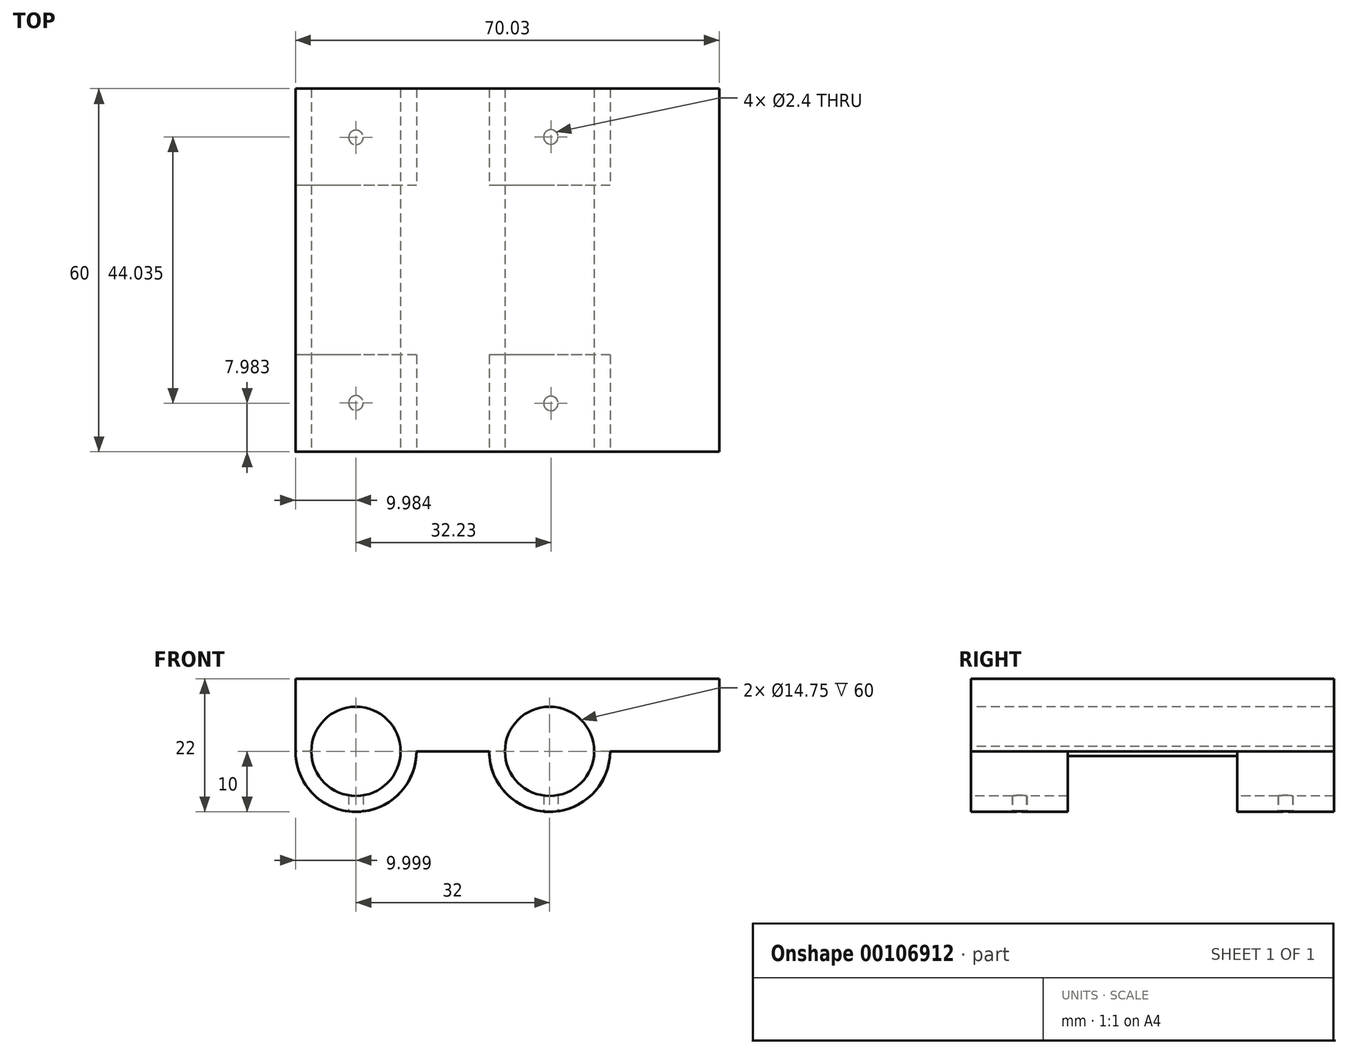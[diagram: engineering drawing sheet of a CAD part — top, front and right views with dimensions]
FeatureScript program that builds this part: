
annotation { "Feature Type Name" : "Feature", "Feature Type Description" : "" }
export const myFeature = defineFeature(function(context is Context, id is Id, definition is map)
    precondition{}
    {
        {
            var Q0;
            Q0=qCreatedBy(makeId("Top.planeOp"),FACE);
            var sketch = newSketch(context, id + "F0", { "sketchPlane" : qUnion([Q0])});
            skLineSegment(sketch, "E0.bottom", {"start": v(35, -30) * mm, "end": v(-35, -30) * mm});
            skLineSegment(sketch, "E0.top", {"start": v(35, 30) * mm, "end": v(-35, 30) * mm});
            skLineSegment(sketch, "E0.left", {"start": v(35, -30) * mm, "end": v(35, 30) * mm});
            skLineSegment(sketch, "E0.right", {"start": v(-35, -30) * mm, "end": v(-35, 30) * mm});
            skPoint(sketch, "E0.middle", {"position": v(0, 0) * mm});
            skSolve(sketch);
        }
        {
            var Q0;
            Q0 = qSketchRegion(id + "F0", true);
            extrude(context, id + "F1", {"entities" : qUnion([Q0]), "depth" : 12 * mm});
        }
        {
            var Q0;
            Q0=makeQuery(id+"F1.opExtrude","SWEPT_FACE",FACE,{"disambiguationData":[OSD([sQuery(id+"F0.wireOp",EDGE,"E0.bottom")])]});
            var sketch = newSketch(context, id + "F2", { "sketchPlane" : qUnion([Q0])});
            skCircle(sketch, "E1", {"center": v(-25.03, 0) * mm, "radius": 10 * mm});
            skCircle(sketch, "E2", {"center": v(6.97, 0) * mm, "radius": 10 * mm});
            skLineSegment(sketch, "E3", {"start": v(-35, 0) * mm, "end": v(-15.03, 0) * mm, "construction": true});
            skLineSegment(sketch, "E4", {"start": v(-3.03, 0) * mm, "end": v(16.97, 0) * mm, "construction": true});
            skCircle(sketch, "E5", {"center": v(-25.03, 0) * mm, "radius": 7.38 * mm});
            skCircle(sketch, "E6", {"center": v(6.97, 0) * mm, "radius": 7.38 * mm});
            skSolve(sketch);
        }
        {
            var Q0;
            {var subQ0=sQuery(id+"F2.wireOp",EDGE,"E5");var subQ1=makeQuery(id+"F1.opExtrude","CAP_EDGE",EDGE,{"disambiguationData":[OSD([sQuery(id+"F0.wireOp",EDGE,"E0.bottom")])],"isStart":true});var subQ2=makeQuery(id+"F2.imprint","INTERSECT",VERTEX,{"disambiguationData":[OD(0.0)],"derivedFrom":[subQ1,subQ0]});Q0=makeQuery(id+"F2.imprint","IMPRINT",FACE,{"disambiguationData":[TD([[makeQuery(id+"F2.imprint","IMPRINT",EDGE,{"disambiguationData":[TD([[subQ2,1.0]])],"derivedFrom":subQ0}),1.0]])]});}
            var Q1;
            {var subQ0=sQuery(id+"F2.wireOp",EDGE,"E6");var subQ1=makeQuery(id+"F1.opExtrude","CAP_EDGE",EDGE,{"disambiguationData":[OSD([sQuery(id+"F0.wireOp",EDGE,"E0.bottom")])],"isStart":true});var subQ2=makeQuery(id+"F2.imprint","INTERSECT",VERTEX,{"disambiguationData":[OD(0.0)],"derivedFrom":[subQ1,subQ0]});Q1=makeQuery(id+"F2.imprint","IMPRINT",FACE,{"disambiguationData":[TD([[makeQuery(id+"F2.imprint","IMPRINT",EDGE,{"disambiguationData":[TD([[subQ2,-1.0]])],"derivedFrom":subQ0}),1.0]])]});}
            extrude(context, id + "F3", {"entities" : qUnion([Q0, Q1]), "operationType" : NewBodyOperationType.REMOVE, "endBound" : BoundingType.THROUGH_ALL, "oppositeDirection" : true, "depth" : 25 * mm});
        }
        {
            var Q0;
            Q0 = qSketchRegion(id + "F2", true);
            var Q1;
            Q1=makeQuery(id+"F1.opExtrude","SWEPT_FACE",FACE,{"disambiguationData":[OSD([sQuery(id+"F0.wireOp",EDGE,"E0.top")])]});
            extrude(context, id + "F4", {"entities" : qUnion([Q0]), "operationType" : NewBodyOperationType.ADD, "endBound" : BoundingType.UP_TO_SURFACE, "oppositeDirection" : true, "endBoundEntityFace" : qUnion([Q1]), "depth" : 25 * mm});
        }
        {
            var Q0;
            Q0=makeQuery(id+"F1.opExtrude","SWEPT_FACE",FACE,{"disambiguationData":[OSD([sQuery(id+"F0.wireOp",EDGE,"E0.right")])]});
            cPlane(context, id + "F5", {"entities" : qUnion([Q0]), "cplaneType" : CPlaneType.OFFSET, "offset" : 0 * mm, "width" : 150 * mm, "height" : 150 * mm});
        }
        {
            var Q0;
            Q0=qCreatedBy(id+"F5.planeOp",FACE);
            var sketch = newSketch(context, id + "F6", { "sketchPlane" : qUnion([Q0])});
            skLineSegment(sketch, "E7.bottom", {"start": v(0, 0) * mm, "end": v(-14, 0) * mm});
            skLineSegment(sketch, "E7.top", {"start": v(0, -16.39) * mm, "end": v(-14, -16.39) * mm});
            skLineSegment(sketch, "E7.left", {"start": v(0, 0) * mm, "end": v(0, -16.39) * mm});
            skLineSegment(sketch, "E7.right", {"start": v(-14, 0) * mm, "end": v(-14, -16.39) * mm});
            skLineSegment(sketch, "E8.MirrorCS", {"start": v(14, 0) * mm, "end": v(14, -16.39) * mm});
            skLineSegment(sketch, "E9.MirrorCS", {"start": v(0, -16.39) * mm, "end": v(14, -16.39) * mm});
            skLineSegment(sketch, "E10.MirrorCS", {"start": v(0, 0) * mm, "end": v(14, 0) * mm});
            skSolve(sketch);
        }
        {
            var Q0;
            Q0 = qSketchRegion(id + "F6", true);
            extrude(context, id + "F7", {"entities" : qUnion([Q0]), "operationType" : NewBodyOperationType.REMOVE, "endBound" : BoundingType.THROUGH_ALL, "oppositeDirection" : true, "depth" : 25 * mm});
        }
        {
            var Q0;
            {var subQ0=sQuery(id+"F0.wireOp",EDGE,"E0.bottom");var subQ1=sQuery(id+"F0.wireOp",EDGE,"E0.top");Q0=makeQuery(id+"F7.boolean.opBoolean","MERGE",FACE,{"derivedFrom":[makeQuery(id+"F3.boolean.opBoolean","SPLIT",FACE,{"disambiguationData":[TD([makeQuery(id+"F1.opExtrude","SWEPT_FACE",FACE,{"disambiguationData":[OSD([subQ0])]}),makeQuery(id+"F1.opExtrude","SWEPT_FACE",FACE,{"disambiguationData":[OSD([subQ1])]}),makeQuery(id+"F3.opExtrude","SWEPT_FACE",FACE,{"disambiguationData":[OSD([sQuery(id+"F2.wireOp",EDGE,"E5")])]}),makeQuery(id+"F3.opExtrude","SWEPT_FACE",FACE,{"disambiguationData":[OSD([sQuery(id+"F2.wireOp",EDGE,"E6")])]})])],"derivedFrom":makeQuery(id+"F1.opExtrude","CAP_FACE",FACE,{"disambiguationData":[OSD([subQ0,subQ1,sQuery(id+"F0.wireOp",EDGE,"E0.left"),sQuery(id+"F0.wireOp",EDGE,"E0.right")])],"isStart":true})}),makeQuery(id+"F7.opExtrude","SWEPT_FACE",FACE,{"disambiguationData":[OSD([sQuery(id+"F6.wireOp",EDGE,"E7.bottom"),sQuery(id+"F6.wireOp",EDGE,"E10.MirrorCS")])]})]});}
            cPlane(context, id + "F8", {"entities" : qUnion([Q0]), "cplaneType" : CPlaneType.OFFSET, "offset" : 10 * mm, "width" : 150 * mm, "height" : 150 * mm});
        }
        {
            var Q0;
            Q0=qCreatedBy(id+"F8.planeOp",FACE);
            var sketch = newSketch(context, id + "F9", { "sketchPlane" : qUnion([Q0])});
            skLineSegment(sketch, "E11", {"start": v(-35.35, 30.04) * mm, "end": v(-14.93, 13.98) * mm, "construction": true});
            skLineSegment(sketch, "E12", {"start": v(-14.93, 13.98) * mm, "end": v(-35.01, 13.98) * mm, "construction": true});
            skLineSegment(sketch, "E13", {"start": v(-35.01, 13.98) * mm, "end": v(-15.1, 29.87) * mm, "construction": true});
            skLineSegment(sketch, "E14", {"start": v(-15.1, 29.87) * mm, "end": v(-14.93, 13.98) * mm, "construction": true});
            skPoint(sketch, "E15", {"position": v(-25.05, 21.94) * mm});
            skLineSegment(sketch, "E16", {"start": v(-3.06, 30.2) * mm, "end": v(17.02, 14.15) * mm, "construction": true});
            skLineSegment(sketch, "E17", {"start": v(17.02, 14.15) * mm, "end": v(-3.06, 14.15) * mm, "construction": true});
            skLineSegment(sketch, "E18", {"start": v(-3.06, 14.15) * mm, "end": v(17.19, 29.7) * mm, "construction": true});
            skLineSegment(sketch, "E19", {"start": v(17.19, 29.7) * mm, "end": v(-3.06, 30.2) * mm, "construction": true});
            skPoint(sketch, "E20", {"position": v(7.18, 22.02) * mm});
            skPoint(sketch, "E21.MirrorP", {"position": v(-25.05, -21.94) * mm});
            skPoint(sketch, "E22.MirrorP", {"position": v(7.18, -22.02) * mm});
            skSolve(sketch);
        }
        {
            var Q0;
            Q0=sQuery(id+"F9.wireOp",VERTEX,"E21.MirrorP");
            var Q1;
            Q1=sQuery(id+"F9.wireOp",VERTEX,"E22.MirrorP");
            var Q2;
            Q2=sQuery(id+"F9.wireOp",VERTEX,"E20");
            var Q3;
            Q3=sQuery(id+"F9.wireOp",VERTEX,"E15");
            var Q4;
            Q4=makeQuery(id+"F1.opExtrude","SWEPT_BODY",BODY,{"disambiguationData":[OSD([sQuery(id+"F0.wireOp",EDGE,"E0.bottom"),sQuery(id+"F0.wireOp",EDGE,"E0.top"),sQuery(id+"F0.wireOp",EDGE,"E0.left"),sQuery(id+"F0.wireOp",EDGE,"E0.right")])]});
            hole(context, id + "F10", {"style" : HoleStyle.SIMPLE, "endStyle" : HoleEndStyle.BLIND, "standardTappedOrClearance" : lookupTablePath({ "standard" : "ISO", "engagement" : "75%", "pitch" : "0.6 mm", "size" : "M3", "type" : "Tapped" }), "standardBlindInLast" : lookupTablePath({ "standard" : "ISO", "engagement" : "75%", "pitch" : "0.6 mm", "size" : "M3", "type" : "Tapped" }), "holeDiameter" : 2.4 * mm, "holeDepth" : 10 * mm, "locations" : qUnion([Q0, Q1, Q2, Q3]), "scope" : qUnion([Q4])});
        }
    });
